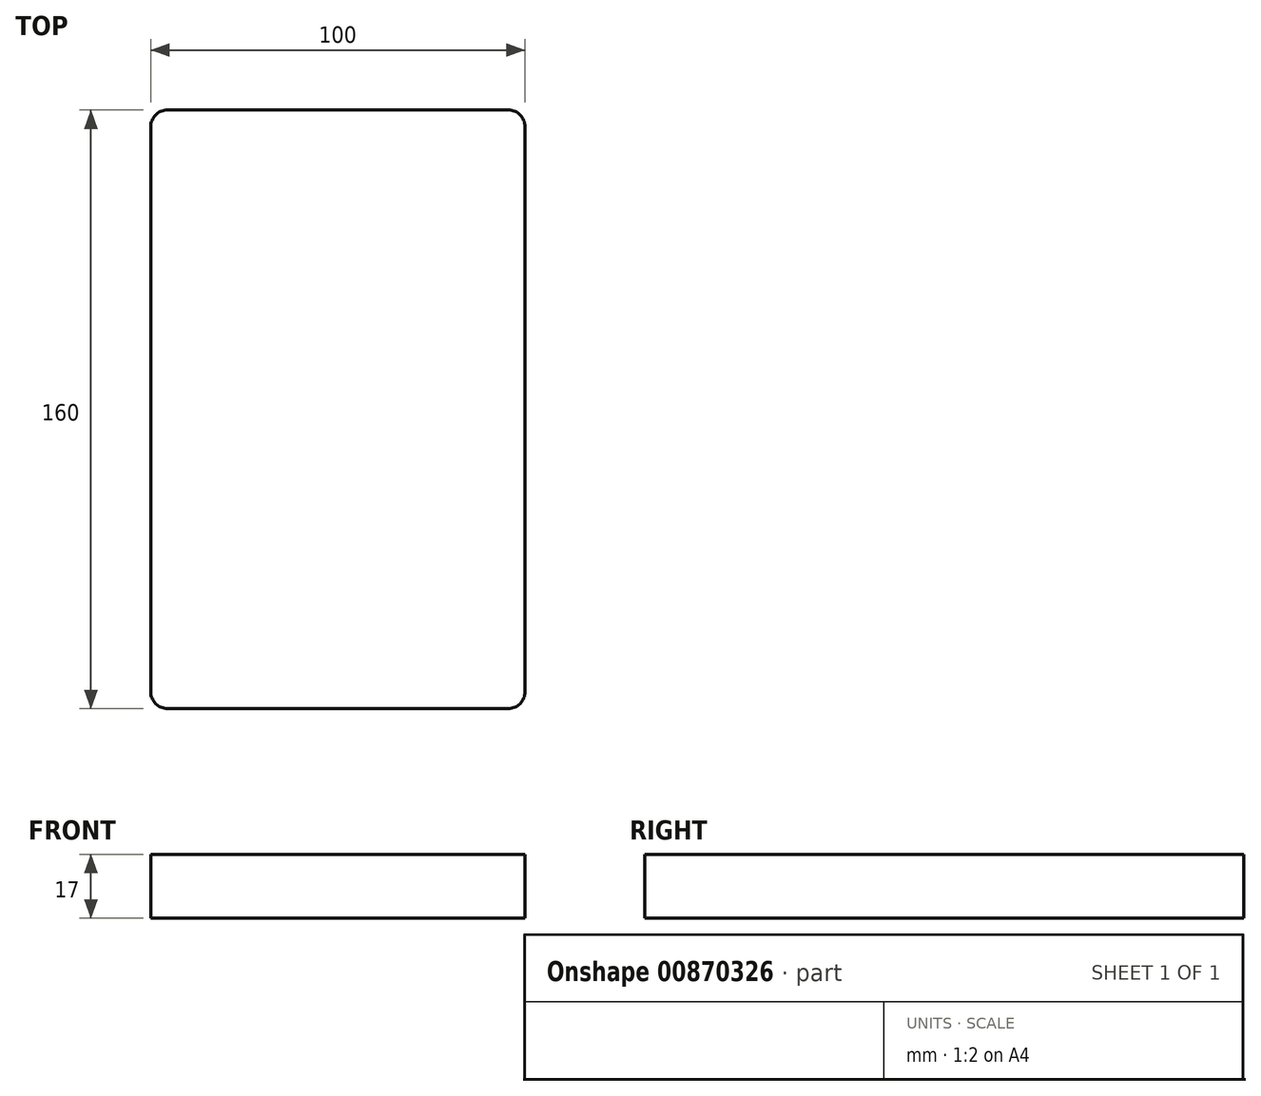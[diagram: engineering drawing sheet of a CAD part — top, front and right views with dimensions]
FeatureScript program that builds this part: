
annotation { "Feature Type Name" : "Feature", "Feature Type Description" : "" }
export const myFeature = defineFeature(function(context is Context, id is Id, definition is map)
    precondition{}
    {
        {
            var Q0;
            Q0=qCreatedBy(makeId("Top.planeOp"),FACE);
            cPlane(context, id + "F0", {"entities" : qUnion([Q0]), "cplaneType" : CPlaneType.OFFSET, "offset" : 17 * mm, "oppositeDirection" : true, "width" : 150 * mm, "height" : 150 * mm});
        }
        {
            var Q0;
            Q0=qCreatedBy(id+"F0.planeOp",FACE);
            var sketch = newSketch(context, id + "F1", { "sketchPlane" : qUnion([Q0])});
            skLineSegment(sketch, "E0.bottom", {"start": v(4.5, 0) * mm, "end": v(50, 0) * mm});
            skLineSegment(sketch, "E0.top", {"start": v(4.5, 160) * mm, "end": v(50, 160) * mm});
            skLineSegment(sketch, "E0.left", {"start": v(0, 4.5) * mm, "end": v(0, 155.5) * mm});
            skLineSegment(sketch, "E0.right", {"start": v(50, 0) * mm, "end": v(50, 160) * mm, "construction": true});
            skPoint(sketch, "E1.visualSharp", {"position": v(0, 160) * mm});
            skArc(sketch, "E1.filletArc", {"start": v(4.5, 160) * mm, "mid": v(1.32, 158.68) * mm, "end": v(0, 155.5) * mm});
            skPoint(sketch, "E2.visualSharp", {"position": v(0, 0) * mm});
            skArc(sketch, "E2.filletArc", {"start": v(0, 4.5) * mm, "mid": v(1.32, 1.32) * mm, "end": v(4.5, 0) * mm});
            skArc(sketch, "E3.MirrorCS", {"start": v(95.5, 160) * mm, "mid": v(98.68, 158.68) * mm, "end": v(100, 155.5) * mm});
            skArc(sketch, "E4.MirrorCS", {"start": v(100, 4.5) * mm, "mid": v(98.68, 1.32) * mm, "end": v(95.5, 0) * mm});
            skLineSegment(sketch, "E5.MirrorCS", {"start": v(100, 4.5) * mm, "end": v(100, 155.5) * mm});
            skPoint(sketch, "E6.MirrorP", {"position": v(100, 0) * mm});
            skLineSegment(sketch, "E7.MirrorCS", {"start": v(95.5, 160) * mm, "end": v(50, 160) * mm});
            skLineSegment(sketch, "E8.MirrorCS", {"start": v(95.5, 0) * mm, "end": v(50, 0) * mm});
            skPoint(sketch, "E9.MirrorP", {"position": v(100, 160) * mm});
            skSolve(sketch);
        }
        {
            var Q0;
            Q0=makeQuery(id+"F1.imprint","IMPRINT",FACE,{"disambiguationData":[TD([[makeQuery(id+"F1.imprint","IMPRINT",EDGE,{"derivedFrom":sQuery(id+"F1.wireOp",EDGE,"E0.bottom")}),1.0]])]});
            extrude(context, id + "F2", {"entities" : qUnion([Q0]), "depth" : 17 * mm, "offsetDistance" : 25 * mm});
        }
    });
